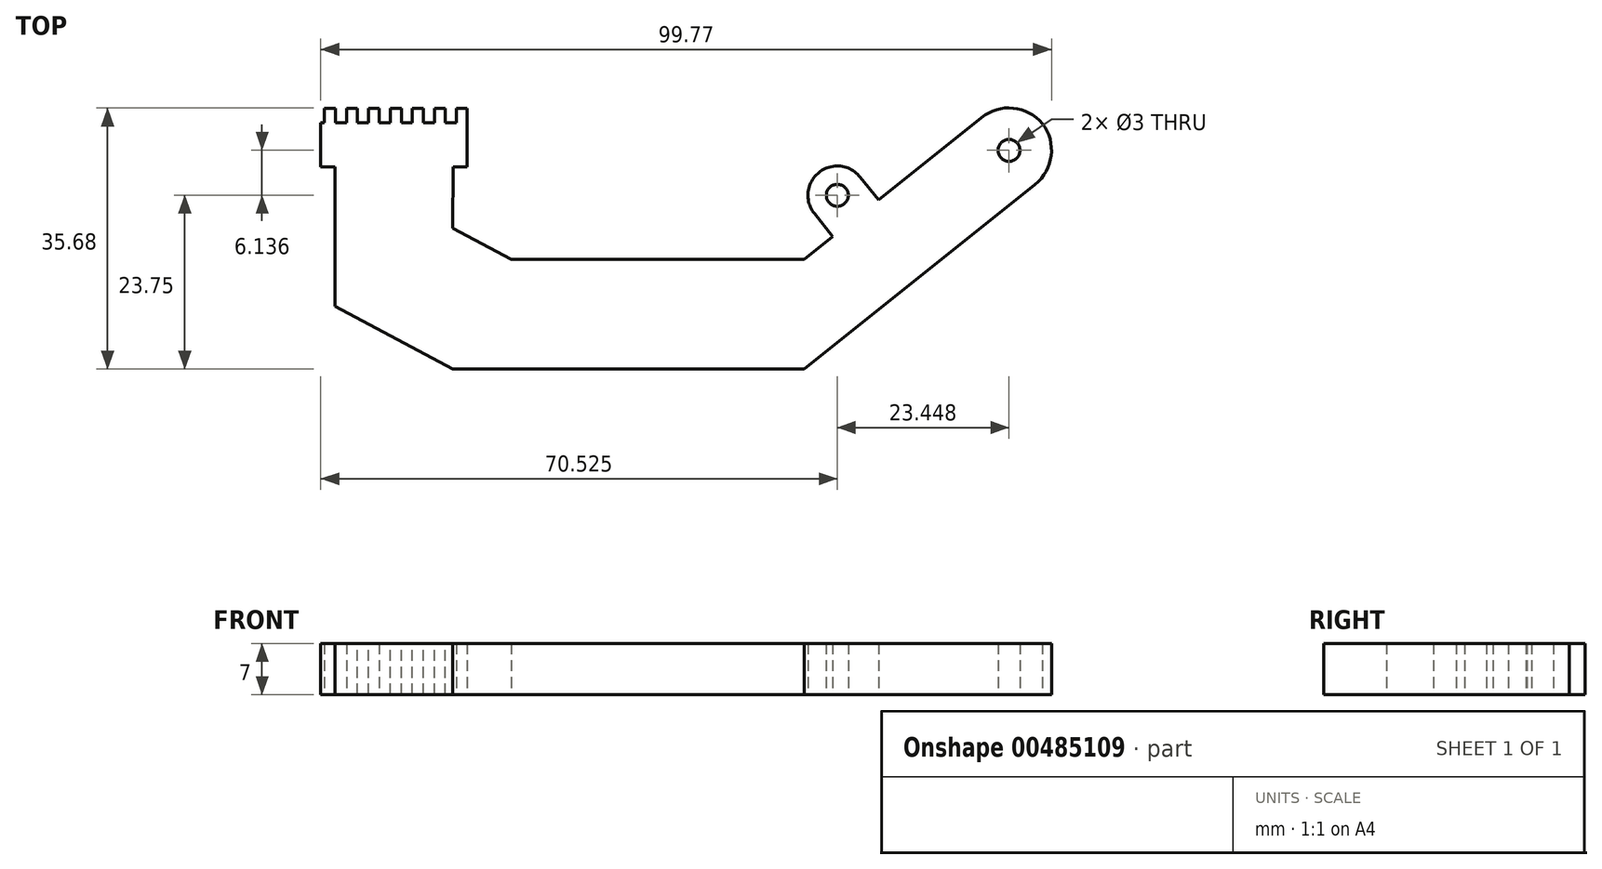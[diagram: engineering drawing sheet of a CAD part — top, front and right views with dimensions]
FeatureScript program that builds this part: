
annotation { "Feature Type Name" : "Feature", "Feature Type Description" : "" }
export const myFeature = defineFeature(function(context is Context, id is Id, definition is map)
    precondition{}
    {
        {
            var Q0;
            Q0=qCreatedBy(makeId("Top.planeOp"),FACE);
            var sketch = newSketch(context, id + "F0", { "sketchPlane" : qUnion([Q0])});
            skPoint(sketch, "E0", {"position": v(-49.3, -30.05) * mm});
            skLineSegment(sketch, "E1.bottom", {"start": v(-79.3, -22.55) * mm, "end": v(-19.3, -22.55) * mm, "construction": true});
            skLineSegment(sketch, "E1.top", {"start": v(-79.3, -37.55) * mm, "end": v(-19.3, -37.55) * mm, "construction": true});
            skLineSegment(sketch, "E1.left", {"start": v(-79.3, -22.55) * mm, "end": v(-79.3, -37.55) * mm, "construction": true});
            skLineSegment(sketch, "E1.right", {"start": v(-19.3, -22.55) * mm, "end": v(-19.3, -37.55) * mm, "construction": true});
            skLineSegment(sketch, "E2", {"start": v(-31.3, -37.55) * mm, "end": v(-31.3, -22.55) * mm, "construction": true});
            skLineSegment(sketch, "E3", {"start": v(-71.3, -37.55) * mm, "end": v(-71.3, -22.55) * mm, "construction": true});
            skLineSegment(sketch, "E4", {"start": v(-19.3, -37.55) * mm, "end": v(-31.3, -22.55) * mm, "construction": true});
            skLineSegment(sketch, "E5", {"start": v(-71.3, -22.55) * mm, "end": v(-79.3, -37.55) * mm, "construction": true});
            skLineSegment(sketch, "E6", {"start": v(-31.3, -22.55) * mm, "end": v(-2.4, 0.57) * mm, "construction": true});
            skLineSegment(sketch, "E7", {"start": v(-19.3, -37.55) * mm, "end": v(9.6, -14.43) * mm, "construction": true});
            skLineSegment(sketch, "E8", {"start": v(-71.3, -22.55) * mm, "end": v(-87.37, -13.97) * mm, "construction": true});
            skLineSegment(sketch, "E9", {"start": v(-79.3, -37.55) * mm, "end": v(-95.36, -28.98) * mm, "construction": true});
            skLineSegment(sketch, "E10", {"start": v(-95.36, -28.98) * mm, "end": v(-87.35, -13.97) * mm, "construction": true});
            skLineSegment(sketch, "E11", {"start": v(-95.36, -28.98) * mm, "end": v(-95.36, -9.92) * mm, "construction": true});
            skLineSegment(sketch, "E12", {"start": v(-95.36, -9.92) * mm, "end": v(-79.22, -9.92) * mm, "construction": true});
            skLineSegment(sketch, "E13", {"start": v(-79.22, -9.92) * mm, "end": v(-79.3, -22.55) * mm, "construction": true});
            skLineSegment(sketch, "E14", {"start": v(-27.39, -19.42) * mm, "end": v(-32.39, -13.18) * mm, "construction": true});
            skLineSegment(sketch, "E15", {"start": v(-21.14, -14.42) * mm, "end": v(-26.14, -8.18) * mm, "construction": true});
            skLineSegment(sketch, "E16", {"start": v(-26.14, -8.18) * mm, "end": v(-32.39, -13.18) * mm, "construction": true});
            skLineSegment(sketch, "E17", {"start": v(-26.14, -8.18) * mm, "end": v(-27.39, -19.42) * mm, "construction": true});
            skLineSegment(sketch, "E18", {"start": v(-32.39, -13.18) * mm, "end": v(-21.14, -14.42) * mm, "construction": true});
            skCircle(sketch, "E19", {"center": v(-26.76, -13.8) * mm, "radius": 1.5 * mm});
            skLineSegment(sketch, "E20", {"start": v(-2.4, 0.57) * mm, "end": v(9.6, -14.43) * mm, "construction": true});
            skLineSegment(sketch, "E21", {"start": v(-31.3, -37.55) * mm, "end": v(4.92, -8.58) * mm, "construction": true});
            skLineSegment(sketch, "E22", {"start": v(-27.39, -19.42) * mm, "end": v(-15.39, -34.42) * mm, "construction": true});
            skLineSegment(sketch, "E23", {"start": v(-21.14, -14.42) * mm, "end": v(-9.14, -29.42) * mm, "construction": true});
            skLineSegment(sketch, "E24", {"start": v(-11.55, -6.75) * mm, "end": v(-4.23, -15.9) * mm, "construction": true});
            skLineSegment(sketch, "E25", {"start": v(-2.4, 0.57) * mm, "end": v(-4.23, -15.9) * mm, "construction": true});
            skLineSegment(sketch, "E26", {"start": v(-11.55, -6.75) * mm, "end": v(4.92, -8.58) * mm, "construction": true});
            skCircle(sketch, "E27", {"center": v(-3.32, -7.66) * mm, "radius": 1.5 * mm});
            skLineSegment(sketch, "E28", {"start": v(-95.36, -9.92) * mm, "end": v(-79.22, -9.92) * mm});
            skLineSegment(sketch, "E29", {"start": v(-95.36, -9.92) * mm, "end": v(-95.36, -28.98) * mm});
            skLineSegment(sketch, "E30", {"start": v(-95.36, -28.98) * mm, "end": v(-79.3, -37.55) * mm});
            skLineSegment(sketch, "E31", {"start": v(-79.3, -37.55) * mm, "end": v(-31.3, -37.55) * mm});
            skLineSegment(sketch, "E32", {"start": v(-31.3, -37.55) * mm, "end": v(4.92, -8.58) * mm});
            skLineSegment(sketch, "E33", {"start": v(4.92, -8.58) * mm, "end": v(-2.4, 0.57) * mm});
            skLineSegment(sketch, "E34", {"start": v(-2.4, 0.57) * mm, "end": v(-21.14, -14.42) * mm});
            skLineSegment(sketch, "E35", {"start": v(-21.14, -14.42) * mm, "end": v(-26.14, -8.18) * mm});
            skLineSegment(sketch, "E36", {"start": v(-26.14, -8.18) * mm, "end": v(-32.39, -13.18) * mm});
            skLineSegment(sketch, "E37", {"start": v(-27.39, -19.42) * mm, "end": v(-32.39, -13.18) * mm});
            skLineSegment(sketch, "E38", {"start": v(-27.39, -19.42) * mm, "end": v(-31.3, -22.55) * mm});
            skLineSegment(sketch, "E39", {"start": v(-31.3, -22.55) * mm, "end": v(-71.3, -22.55) * mm});
            skLineSegment(sketch, "E40", {"start": v(-71.3, -22.55) * mm, "end": v(-79.27, -18.3) * mm});
            skLineSegment(sketch, "E41", {"start": v(-79.27, -18.3) * mm, "end": v(-79.22, -9.92) * mm});
            skSolve(sketch);
        }
        {
            var Q0;
            Q0=makeQuery(id+"F0.imprint","IMPRINT",FACE,{"disambiguationData":[TD([[makeQuery(id+"F0.imprint","IMPRINT",EDGE,{"derivedFrom":sQuery(id+"F0.wireOp",EDGE,"E19")}),-1.0]])]});
            extrude(context, id + "F1", {"entities" : qUnion([Q0]), "depth" : 7 * mm, "offsetDistance" : 25 * mm});
        }
        {
            var Q0;
            Q0=makeQuery(id+"F1.opExtrude","SWEPT_EDGE",EDGE,{"disambiguationData":[OSD([sQuery(id+"F0.wireOp",EDGE,"E35"),sQuery(id+"F0.wireOp",EDGE,"E36")])]});
            var Q1;
            Q1=makeQuery(id+"F1.opExtrude","SWEPT_EDGE",EDGE,{"disambiguationData":[OSD([sQuery(id+"F0.wireOp",EDGE,"E36"),sQuery(id+"F0.wireOp",EDGE,"E37")])]});
            fillet(context, id + "F2", {"entities" : qUnion([Q0, Q1]), "radius" : 4 * mm, "tangentPropagation" : true, "allowEdgeOverflow" : false});
        }
        {
            var Q0;
            Q0=makeQuery(id+"F1.opExtrude","SWEPT_EDGE",EDGE,{"disambiguationData":[OSD([sQuery(id+"F0.wireOp",EDGE,"E33"),sQuery(id+"F0.wireOp",EDGE,"E34")])]});
            var Q1;
            Q1=makeQuery(id+"F1.opExtrude","SWEPT_EDGE",EDGE,{"disambiguationData":[OSD([sQuery(id+"F0.wireOp",EDGE,"E32"),sQuery(id+"F0.wireOp",EDGE,"E33")])]});
            fillet(context, id + "F3", {"entities" : qUnion([Q0, Q1]), "radius" : 6 * mm, "tangentPropagation" : true, "allowEdgeOverflow" : false});
        }
        {
            var Q0;
            Q0=makeQuery(id+"F1.opExtrude","SWEPT_FACE",FACE,{"disambiguationData":[OSD([sQuery(id+"F0.wireOp",EDGE,"E28")])]});
            var sketch = newSketch(context, id + "F4", { "sketchPlane" : qUnion([Q0])});
            skLineSegment(sketch, "E42.bottom", {"start": v(79.22, 7) * mm, "end": v(95.36, 7) * mm, "construction": true});
            skLineSegment(sketch, "E42.top", {"start": v(79.22, 0) * mm, "end": v(95.36, 0) * mm, "construction": true});
            skLineSegment(sketch, "E42.left", {"start": v(79.22, 7) * mm, "end": v(79.22, 0) * mm, "construction": true});
            skLineSegment(sketch, "E42.right", {"start": v(95.36, 7) * mm, "end": v(95.36, 0) * mm, "construction": true});
            skLineSegment(sketch, "E43", {"start": v(77.29, 0) * mm, "end": v(97.29, 0) * mm});
            skLineSegment(sketch, "E44", {"start": v(97.29, 0) * mm, "end": v(97.29, 7) * mm});
            skLineSegment(sketch, "E45", {"start": v(97.29, 7) * mm, "end": v(77.29, 7) * mm});
            skLineSegment(sketch, "E46", {"start": v(77.29, 7) * mm, "end": v(77.29, 0) * mm});
            skLineSegment(sketch, "E47", {"start": v(87.29, 0) * mm, "end": v(87.29, 7) * mm, "construction": true});
            skSolve(sketch);
        }
        {
            var Q0;
            Q0 = qSketchRegion(id + "F4", true);
            extrude(context, id + "F5", {"entities" : qUnion([Q0]), "operationType" : NewBodyOperationType.ADD, "depth" : 6 * mm, "offsetDistance" : 25 * mm});
        }
        {
            var Q0;
            Q0=makeQuery(id+"F5.opExtrude","CAP_FACE",FACE,{"disambiguationData":[OSD([sQuery(id+"F4.wireOp",EDGE,"E43"),sQuery(id+"F4.wireOp",EDGE,"E44"),sQuery(id+"F4.wireOp",EDGE,"E45"),sQuery(id+"F4.wireOp",EDGE,"E46")])],"isStart":false});
            var sketch = newSketch(context, id + "F6", { "sketchPlane" : qUnion([Q0])});
            skLineSegment(sketch, "E48.bottom", {"start": v(77.29, 7) * mm, "end": v(97.29, 7) * mm});
            skLineSegment(sketch, "E48.top", {"start": v(77.29, 0) * mm, "end": v(97.29, 0) * mm});
            skLineSegment(sketch, "E48.left", {"start": v(77.29, 7) * mm, "end": v(77.29, 0) * mm});
            skLineSegment(sketch, "E48.right", {"start": v(97.29, 7) * mm, "end": v(97.29, 0) * mm});
            skLineSegment(sketch, "E49", {"start": v(78.79, 7) * mm, "end": v(78.79, 0) * mm});
            skLineSegment(sketch, "E50", {"start": v(80.29, 0) * mm, "end": v(80.29, 7) * mm});
            skLineSegment(sketch, "E51", {"start": v(81.79, 0) * mm, "end": v(81.79, 7) * mm});
            skLineSegment(sketch, "E52", {"start": v(83.29, 0) * mm, "end": v(83.29, 7) * mm});
            skLineSegment(sketch, "E53", {"start": v(84.79, 0) * mm, "end": v(84.79, 7) * mm});
            skLineSegment(sketch, "E54", {"start": v(86.29, 0) * mm, "end": v(86.29, 7) * mm});
            skLineSegment(sketch, "E55", {"start": v(87.79, 0) * mm, "end": v(87.79, 7) * mm});
            skLineSegment(sketch, "E56", {"start": v(90.79, 0) * mm, "end": v(90.79, 7) * mm});
            skLineSegment(sketch, "E57", {"start": v(89.29, 7) * mm, "end": v(89.29, 0) * mm});
            skLineSegment(sketch, "E58", {"start": v(92.29, 0) * mm, "end": v(92.29, 7) * mm});
            skLineSegment(sketch, "E59", {"start": v(93.79, 7) * mm, "end": v(93.79, 0) * mm});
            skLineSegment(sketch, "E60", {"start": v(95.29, 0) * mm, "end": v(95.29, 7) * mm});
            skLineSegment(sketch, "E61", {"start": v(96.79, 7) * mm, "end": v(96.79, 0) * mm});
            skSolve(sketch);
        }
        {
            var Q0;
            {var subQ0=sQuery(id+"F6.wireOp",EDGE,"E48.left");Q0=makeQuery(id+"F6.imprint","IMPRINT",FACE,{"disambiguationData":[TD([[makeQuery(id+"F6.imprint","IMPRINT",EDGE,{"derivedFrom":subQ0}),1.0]])]});}
            var Q1;
            {var subQ0=sQuery(id+"F6.wireOp",EDGE,"E50");Q1=makeQuery(id+"F6.imprint","IMPRINT",FACE,{"disambiguationData":[TD([[makeQuery(id+"F6.imprint","IMPRINT",EDGE,{"derivedFrom":subQ0}),-1.0]])]});}
            var Q2;
            {var subQ0=sQuery(id+"F6.wireOp",EDGE,"E52");Q2=makeQuery(id+"F6.imprint","IMPRINT",FACE,{"disambiguationData":[TD([[makeQuery(id+"F6.imprint","IMPRINT",EDGE,{"derivedFrom":subQ0}),-1.0]])]});}
            var Q3;
            {var subQ0=sQuery(id+"F6.wireOp",EDGE,"E54");Q3=makeQuery(id+"F6.imprint","IMPRINT",FACE,{"disambiguationData":[TD([[makeQuery(id+"F6.imprint","IMPRINT",EDGE,{"derivedFrom":subQ0}),-1.0]])]});}
            var Q4;
            {var subQ0=sQuery(id+"F6.wireOp",EDGE,"E56");Q4=makeQuery(id+"F6.imprint","IMPRINT",FACE,{"disambiguationData":[TD([[makeQuery(id+"F6.imprint","IMPRINT",EDGE,{"derivedFrom":subQ0}),1.0]])]});}
            var Q5;
            {var subQ0=sQuery(id+"F6.wireOp",EDGE,"E58");Q5=makeQuery(id+"F6.imprint","IMPRINT",FACE,{"disambiguationData":[TD([[makeQuery(id+"F6.imprint","IMPRINT",EDGE,{"derivedFrom":subQ0}),-1.0]])]});}
            var Q6;
            {var subQ0=sQuery(id+"F6.wireOp",EDGE,"E60");Q6=makeQuery(id+"F6.imprint","IMPRINT",FACE,{"disambiguationData":[TD([[makeQuery(id+"F6.imprint","IMPRINT",EDGE,{"derivedFrom":subQ0}),-1.0]])]});}
            extrude(context, id + "F7", {"entities" : qUnion([Q0, Q1, Q2, Q3, Q4, Q5, Q6]), "operationType" : NewBodyOperationType.ADD, "depth" : 2 * mm, "offsetDistance" : 25 * mm});
        }
    });
